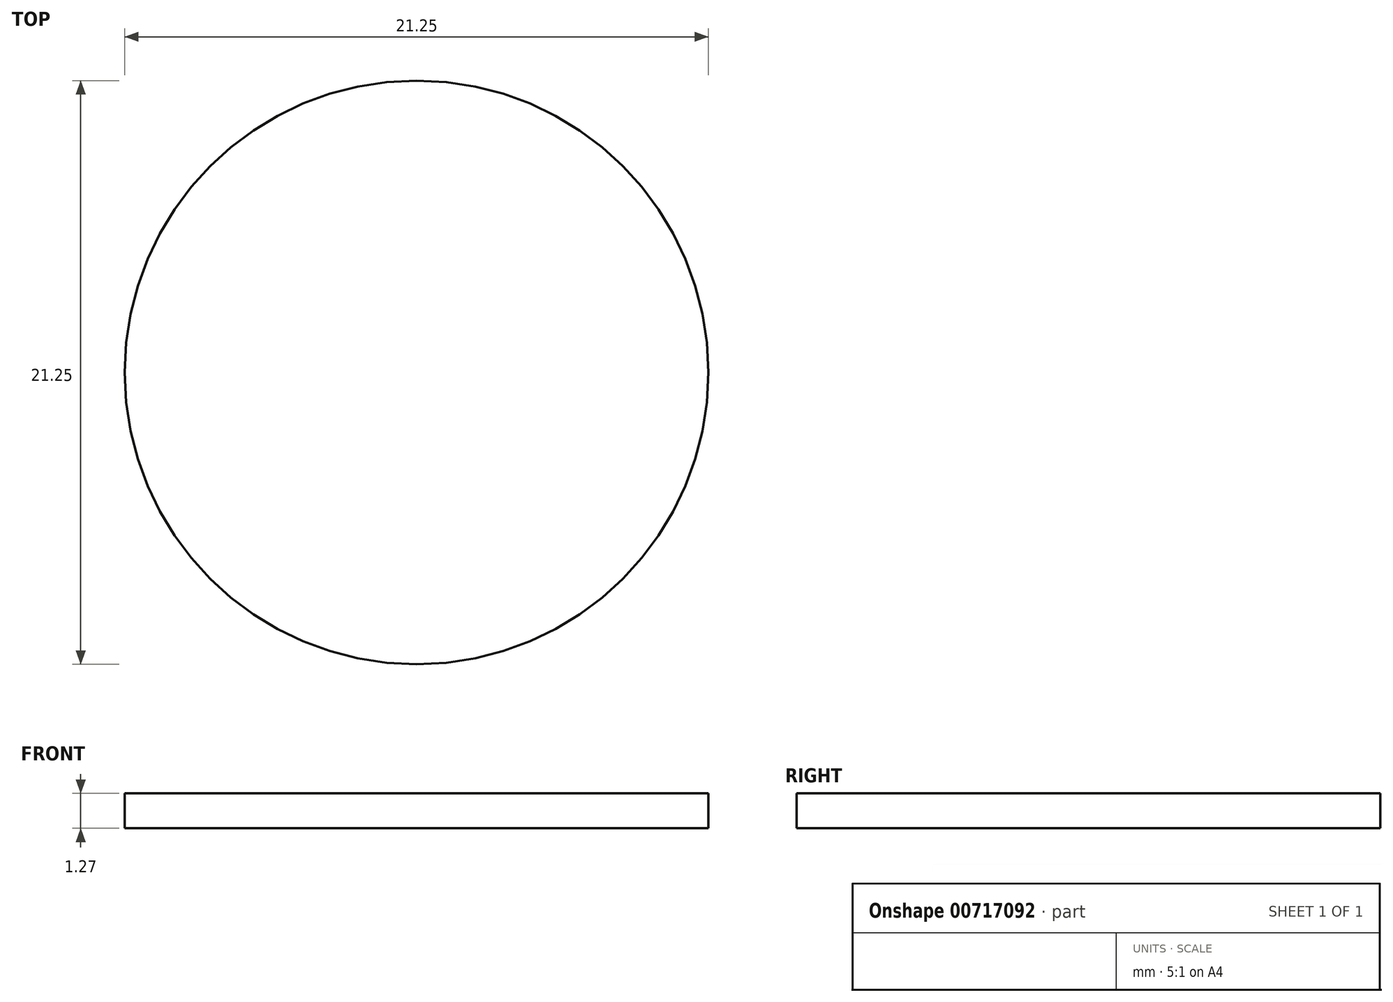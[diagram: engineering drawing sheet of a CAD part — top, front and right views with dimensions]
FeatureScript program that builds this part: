
annotation { "Feature Type Name" : "Feature", "Feature Type Description" : "" }
export const myFeature = defineFeature(function(context is Context, id is Id, definition is map)
    precondition{}
    {
        {
            var Q0;
            Q0=qCreatedBy(makeId("Top.planeOp"),FACE);
            var sketch = newSketch(context, id + "F0", { "sketchPlane" : qUnion([Q0])});
            skCircle(sketch, "E0", {"center": v(-64.28, -55.94) * mm, "radius": 10.62 * mm});
            skSolve(sketch);
        }
        {
            var Q0;
            Q0 = qSketchRegion(id + "F0", true);
            extrude(context, id + "F1", {"entities" : qUnion([Q0]), "depth" : 1.27 * mm, "offsetDistance" : 25.4 * mm});
        }
    });
